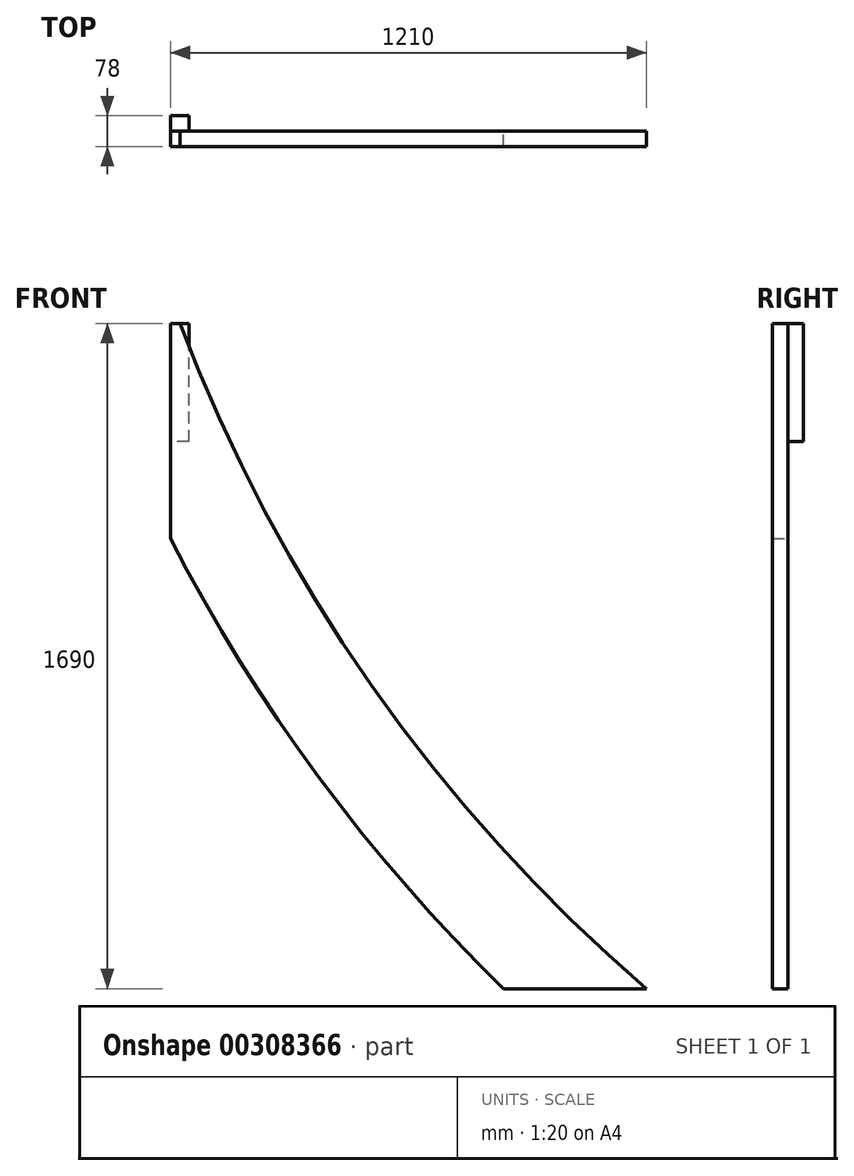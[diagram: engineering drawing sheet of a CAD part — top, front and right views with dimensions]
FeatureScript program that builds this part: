
annotation { "Feature Type Name" : "Feature", "Feature Type Description" : "" }
export const myFeature = defineFeature(function(context is Context, id is Id, definition is map)
    precondition{}
    {
        {
            var Q0;
            Q0=qCreatedBy(makeId("Front.planeOp"),FACE);
            var sketch = newSketch(context, id + "F0", { "sketchPlane" : qUnion([Q0])});
            skLineSegment(sketch, "E0.bottom", {"start": v(0, 0) * mm, "end": v(-363.18, 0) * mm});
            skLineSegment(sketch, "E0.top", {"start": v(-1185, 1690) * mm, "end": v(-1210, 1690) * mm});
            skLineSegment(sketch, "E0.right", {"start": v(-1210, 1143.75) * mm, "end": v(-1210, 1690) * mm});
            skArc(sketch, "E1", {"start": v(-1185, 1690) * mm, "mid": v(-698.94, 770.37) * mm, "end": v(0, 0) * mm});
            skArc(sketch, "E2.0", {"start": v(-1210, 1143.75) * mm, "mid": v(-833.07, 537.46) * mm, "end": v(-363.18, 0) * mm});
            skSolve(sketch);
        }
        {
            var Q0;
            Q0 = qSketchRegion(id + "F0", true);
            extrude(context, id + "F1", {"entities" : qUnion([Q0]), "depth" : 39 * mm});
        }
        {
            var Q0;
            Q0=makeQuery(id+"F1.opExtrude","SWEPT_FACE",FACE,{"disambiguationData":[OSD([sQuery(id+"F0.wireOp",EDGE,"E0.top")])]});
            var sketch = newSketch(context, id + "F2", { "sketchPlane" : qUnion([Q0])});
            skLineSegment(sketch, "E3.bottom", {"start": v(-1210, 0) * mm, "end": v(-1163, 0) * mm});
            skLineSegment(sketch, "E3.top", {"start": v(-1210, 39) * mm, "end": v(-1163, 39) * mm});
            skLineSegment(sketch, "E3.left", {"start": v(-1210, 0) * mm, "end": v(-1210, 39) * mm});
            skLineSegment(sketch, "E3.right", {"start": v(-1163, 0) * mm, "end": v(-1163, 39) * mm});
            skSolve(sketch);
        }
        {
            var Q0;
            Q0=makeQuery(id+"F2.imprint","IMPRINT",FACE,{"disambiguationData":[TD([[makeQuery(id+"F2.imprint","IMPRINT",EDGE,{"derivedFrom":sQuery(id+"F2.wireOp",EDGE,"E3.top")}),-1.0]])]});
            extrude(context, id + "F3", {"entities" : qUnion([Q0]), "oppositeDirection" : true, "depth" : 300 * mm});
        }
    });
